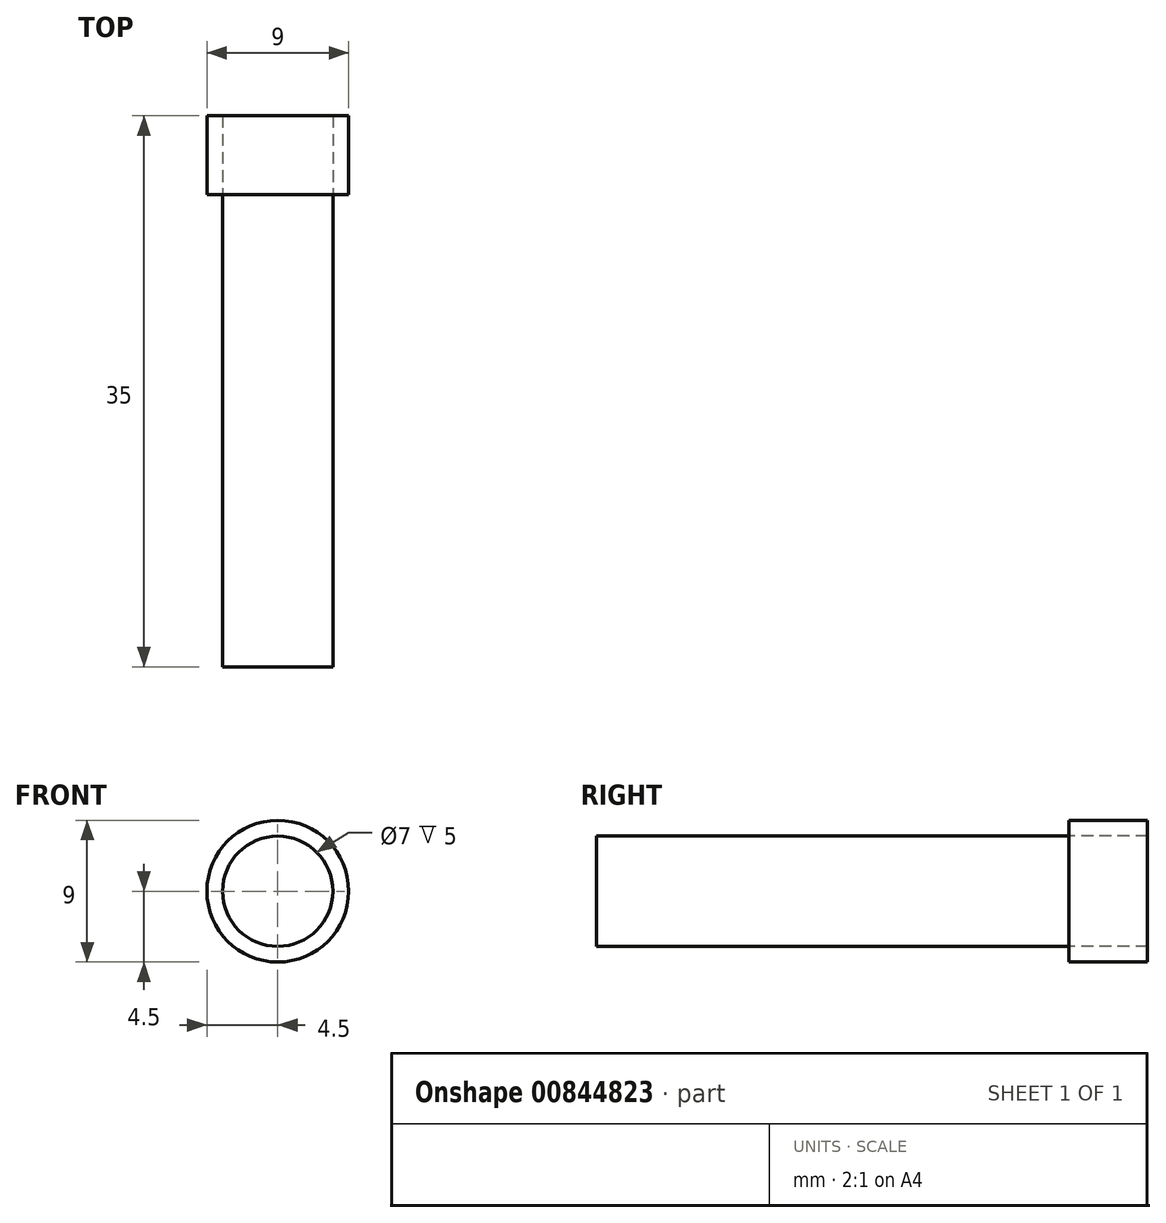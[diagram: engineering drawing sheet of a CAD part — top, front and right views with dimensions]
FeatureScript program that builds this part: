
annotation { "Feature Type Name" : "Feature", "Feature Type Description" : "" }
export const myFeature = defineFeature(function(context is Context, id is Id, definition is map)
    precondition{}
    {
        {
            var Q0;
            Q0=qCreatedBy(makeId("Front.planeOp"),FACE);
            var sketch = newSketch(context, id + "F0", { "sketchPlane" : qUnion([Q0])});
            skCircle(sketch, "E0", {"center": v(0, 0) * mm, "radius": 3.5 * mm});
            skSolve(sketch);
        }
        {
            var Q0;
            Q0=makeQuery(id+"F0.imprint","IMPRINT",FACE,{"disambiguationData":[TD([[makeQuery(id+"F0.imprint","IMPRINT",EDGE,{"derivedFrom":sQuery(id+"F0.wireOp",EDGE,"E0")}),1.0]])]});
            extrude(context, id + "F1", {"entities" : qUnion([Q0]), "depth" : 30 * mm, "offsetDistance" : 25 * mm});
        }
        {
            var Q0;
            Q0=makeQuery(id+"F1.opExtrude","CAP_FACE",FACE,{"disambiguationData":[OSD([sQuery(id+"F0.wireOp",EDGE,"E0")])],"isStart":true});
            var sketch = newSketch(context, id + "F2", { "sketchPlane" : qUnion([Q0])});
            skCircle(sketch, "E1", {"center": v(0, 0) * mm, "radius": 3 * mm});
            skCircle(sketch, "E2", {"center": v(0, 0) * mm, "radius": 4.5 * mm});
            skSolve(sketch);
        }
        {
            var Q0;
            Q0=makeQuery(id+"F2.imprint","IMPRINT",FACE,{"disambiguationData":[TD([[makeQuery(id+"F2.imprint","IMPRINT",EDGE,{"derivedFrom":sQuery(id+"F2.wireOp",EDGE,"E2")}),1.0]])]});
            extrude(context, id + "F3", {"entities" : qUnion([Q0]), "depth" : 5 * mm, "offsetDistance" : 25 * mm});
        }
    });
